# Revit family: Haworth_ComposeEcho_HeightAdjustTable_Rectangular
name_source: partatom
category: Furniture Systems
units: mm (PartAtom-declared; Revit-internal decimal feet)

## family parameters
Always vertical = Yes
Cut with Voids When Loaded = No
OmniClass Number = 23.40.70.14.64.21
OmniClass Title = Systems Furniture
Part Type = Normal
Room Calculation Point = No
Round Connector Dimension = Use Diameter
Shared = No
Work Plane-Based = No

## types (3) — shared parameters
Actual Depth = 29 "
Assembly Code = E2020200
Depth = 29 "
Description = Haworth - Compose Echo HAT Rectangular
Manufacturer = Haworth
Max. Depth = 29 "
Max. Height = 46 "
Max. Width = 58 "
Min. Depth = 23 "
Min. Height = 27 "
Min. Width = 46 "
Min/Max Width = 46-70 in.
Model = Haworth - Compose Echo HAT Rectangular
Revision Number = 1
Size = Verify Final Dim. w/ Haworth
Standard Depths = 29 in.
Sustainability Info = https://www.haworth.com
URL = www.haworth.com
URL - Product = https://www.haworth.com
Warranty = http://www.haworth.com

## per-type parameters (varying)
| type | Actual Width | Floor Component Width | Rail Length | Screen Width | Tether Length | Understructure Width | Width |
| 54w 29d | 54 " | 26.26 " | 26.5 " | 42 " | 28.489 " | 32 " | 54 " |
| 58w 29d | 58 " | 26.26 " | 28.5 " | 46 " | 30.489 " | 36 " | 58 " |
| 46w 29d | 46 " | 18.26 " | 22.5 " | 34 " | 24.489 " | 24 " | 46 " |

## geometry (parser evidence)
native form markers: Sweep x66
no freeform markers — native parametric forms only
